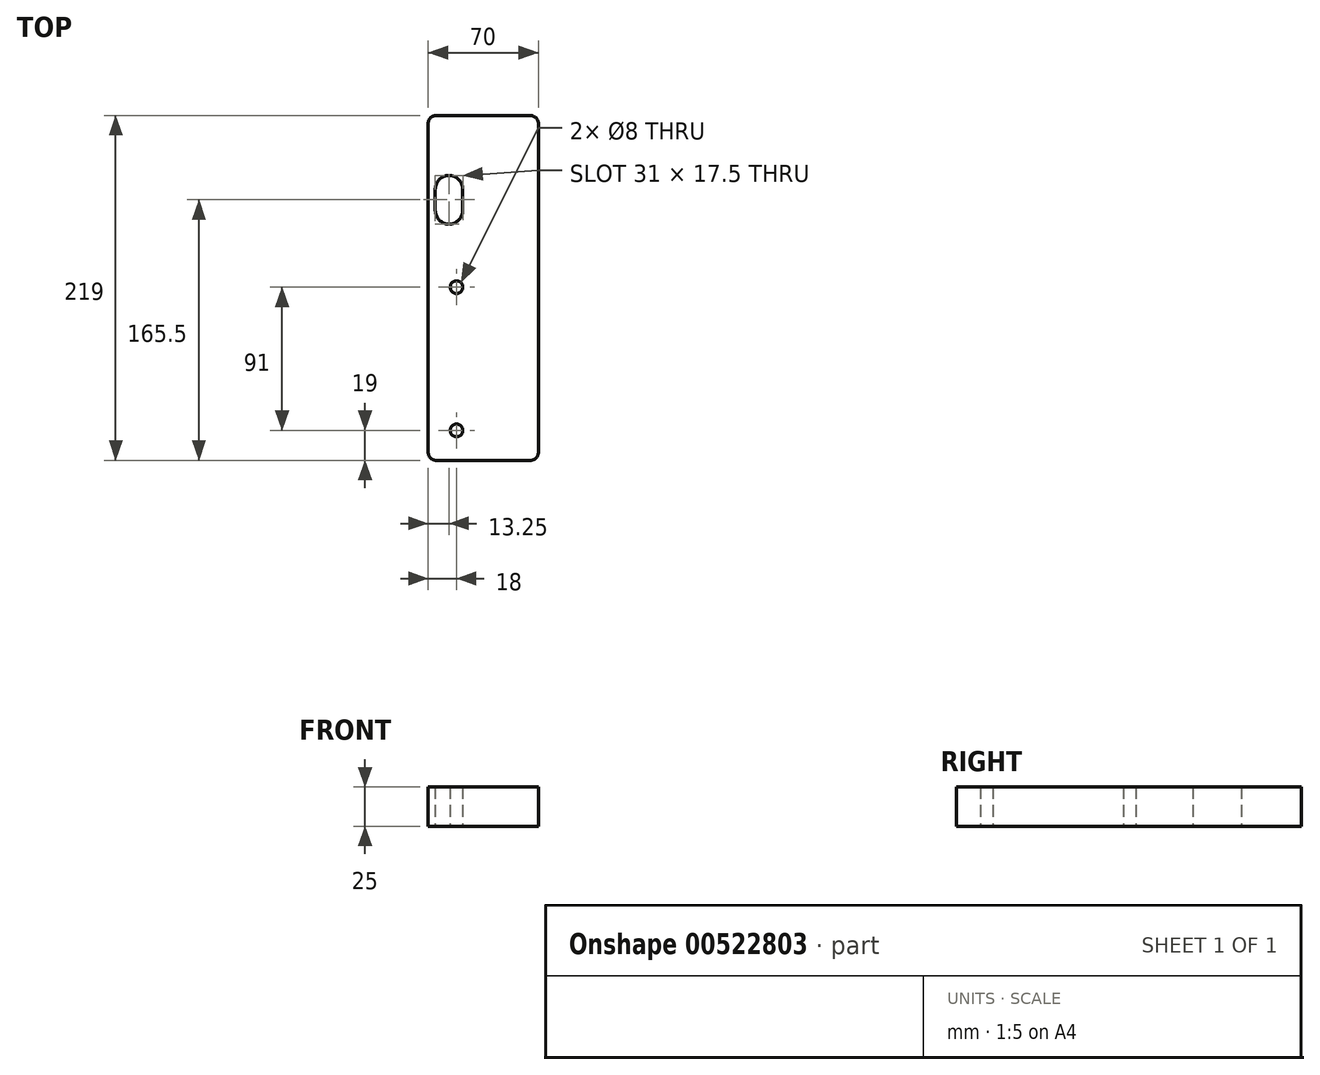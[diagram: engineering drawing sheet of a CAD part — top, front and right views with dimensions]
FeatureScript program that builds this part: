
annotation { "Feature Type Name" : "Feature", "Feature Type Description" : "" }
export const myFeature = defineFeature(function(context is Context, id is Id, definition is map)
    precondition{}
    {
        {
            var Q0;
            Q0=qCreatedBy(makeId("Top.planeOp"),FACE);
            var sketch = newSketch(context, id + "F0", { "sketchPlane" : qUnion([Q0])});
            skLineSegment(sketch, "E0.bottom", {"start": v(-30, -109.5) * mm, "end": v(30, -109.5) * mm});
            skLineSegment(sketch, "E0.top", {"start": v(-30, 109.5) * mm, "end": v(30, 109.5) * mm});
            skLineSegment(sketch, "E0.left", {"start": v(-35, -104.5) * mm, "end": v(-35, 104.5) * mm});
            skLineSegment(sketch, "E0.right", {"start": v(35, -104.5) * mm, "end": v(35, 104.5) * mm});
            skPoint(sketch, "E0.middle", {"position": v(0, 0) * mm});
            skLineSegment(sketch, "E1", {"start": v(-21.75, 109.5) * mm, "end": v(-21.75, -109.5) * mm, "construction": true});
            skArc(sketch, "E2", {"start": v(-13, 62.75) * mm, "mid": v(-21.75, 71.5) * mm, "end": v(-30.5, 62.75) * mm});
            skArc(sketch, "E3", {"start": v(-30.5, 49.25) * mm, "mid": v(-21.75, 40.5) * mm, "end": v(-13, 49.25) * mm});
            skLineSegment(sketch, "E4", {"start": v(-30.5, 62.75) * mm, "end": v(-30.5, 49.25) * mm});
            skLineSegment(sketch, "E5", {"start": v(-13, 49.25) * mm, "end": v(-13, 62.75) * mm});
            skLineSegment(sketch, "E6", {"start": v(-17, -109.5) * mm, "end": v(-17, 109.5) * mm, "construction": true});
            skCircle(sketch, "E7", {"center": v(-17, 0.5) * mm, "radius": 4 * mm});
            skCircle(sketch, "E8", {"center": v(-17, -90.5) * mm, "radius": 4 * mm});
            skPoint(sketch, "E9.visualSharp", {"position": v(35, 109.5) * mm});
            skArc(sketch, "E9.filletArc", {"start": v(35, 104.5) * mm, "mid": v(33.54, 108.04) * mm, "end": v(30, 109.5) * mm});
            skPoint(sketch, "E10.visualSharp", {"position": v(-35, 109.5) * mm});
            skArc(sketch, "E10.filletArc", {"start": v(-30, 109.5) * mm, "mid": v(-33.54, 108.04) * mm, "end": v(-35, 104.5) * mm});
            skPoint(sketch, "E11.visualSharp", {"position": v(-35, -109.5) * mm});
            skArc(sketch, "E11.filletArc", {"start": v(-35, -104.5) * mm, "mid": v(-33.54, -108.04) * mm, "end": v(-30, -109.5) * mm});
            skPoint(sketch, "E12.visualSharp", {"position": v(35, -109.5) * mm});
            skArc(sketch, "E12.filletArc", {"start": v(30, -109.5) * mm, "mid": v(33.54, -108.04) * mm, "end": v(35, -104.5) * mm});
            skSolve(sketch);
        }
        {
            var Q0;
            Q0 = qSketchRegion(id + "F0", true);
            extrude(context, id + "F1", {"entities" : qUnion([Q0]), "depth" : 25 * mm, "offsetDistance" : 25 * mm});
        }
    });
